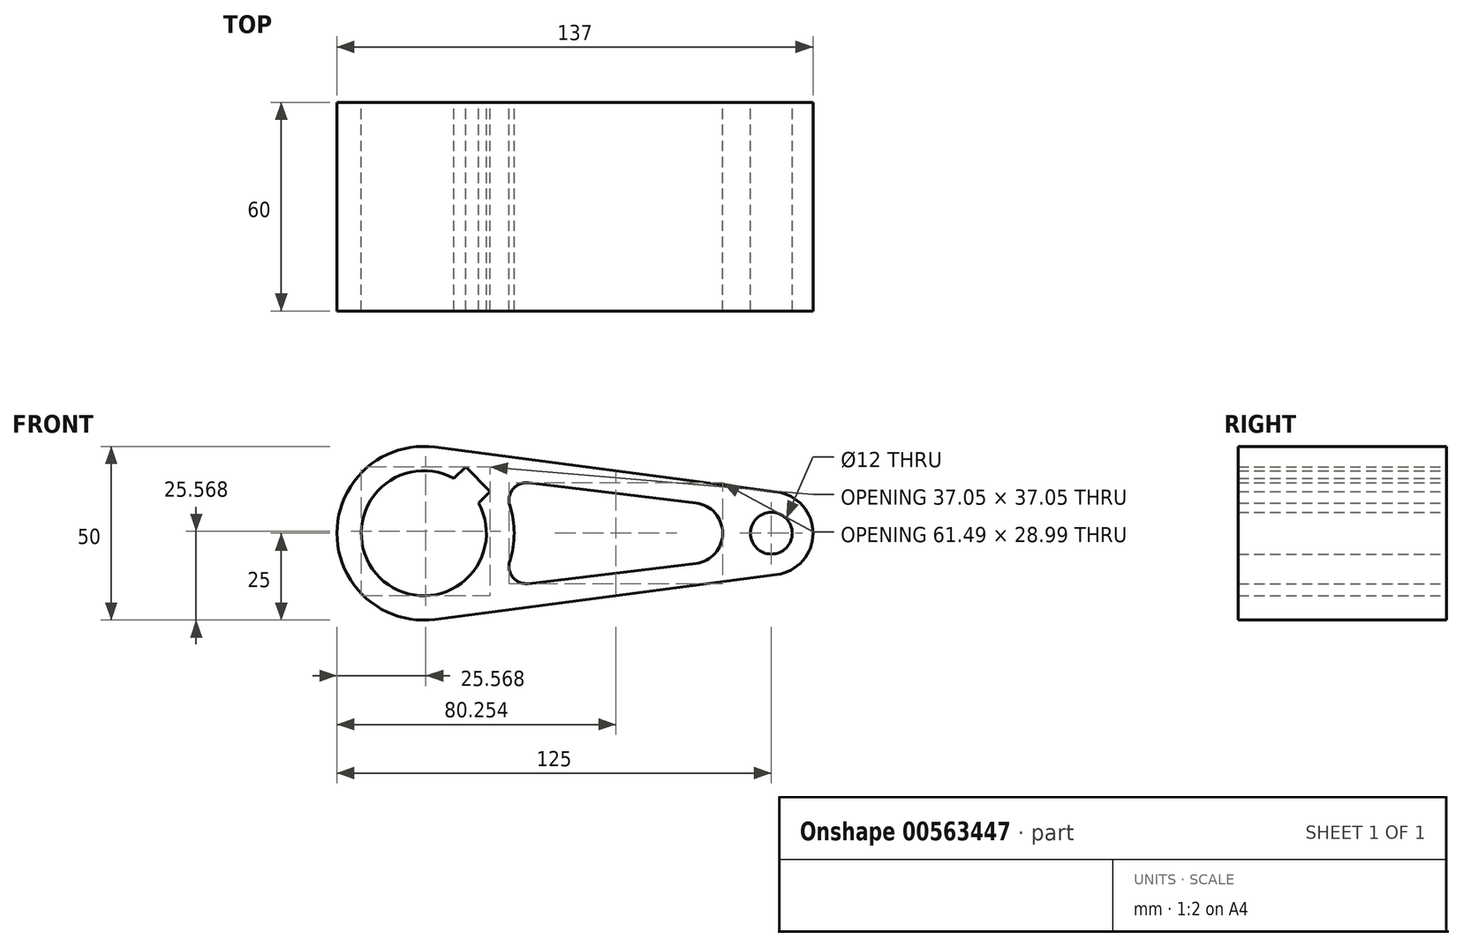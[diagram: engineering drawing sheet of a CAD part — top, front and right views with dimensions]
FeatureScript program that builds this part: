
annotation { "Feature Type Name" : "Feature", "Feature Type Description" : "" }
export const myFeature = defineFeature(function(context is Context, id is Id, definition is map)
    precondition{}
    {
        {
            var Q0;
            Q0=qCreatedBy(makeId("Front.planeOp"),FACE);
            var sketch = newSketch(context, id + "F0", { "sketchPlane" : qUnion([Q0])});
            skArc(sketch, "E0", {"start": v(3.25, 24.79) * mm, "mid": v(-25, 0) * mm, "end": v(3.25, -24.79) * mm});
            skArc(sketch, "E1", {"start": v(101.56, -11.9) * mm, "mid": v(112, 0) * mm, "end": v(101.56, 11.9) * mm});
            skLineSegment(sketch, "E2", {"start": v(3.25, 24.79) * mm, "end": v(101.56, 11.9) * mm});
            skLineSegment(sketch, "E3", {"start": v(3.25, -24.79) * mm, "end": v(101.56, -11.9) * mm});
            skLineSegment(sketch, "E4", {"start": v(0, 0) * mm, "end": v(15.56, 15.56) * mm, "construction": true});
            skLineSegment(sketch, "E5", {"start": v(15.56, 15.56) * mm, "end": v(19.1, 12.02) * mm});
            skLineSegment(sketch, "E6.MirrorCS", {"start": v(15.56, 15.56) * mm, "end": v(12.02, 19.1) * mm});
            skArc(sketch, "E7", {"start": v(8.7, 15.76) * mm, "mid": v(-12.73, -12.73) * mm, "end": v(15.76, 8.7) * mm});
            skLineSegment(sketch, "E8", {"start": v(12.02, 19.1) * mm, "end": v(8.7, 15.76) * mm});
            skLineSegment(sketch, "E9", {"start": v(19.1, 12.02) * mm, "end": v(15.76, 8.7) * mm});
            skCircle(sketch, "E10", {"center": v(100, 0) * mm, "radius": 6 * mm});
            skLineSegment(sketch, "E11", {"start": v(0, 0) * mm, "end": v(100, 0) * mm, "construction": true});
            skLineSegment(sketch, "E12", {"start": v(30.1, 14.5) * mm, "end": v(78.32, 8.66) * mm});
            skLineSegment(sketch, "E13", {"start": v(30.1, -14.5) * mm, "end": v(78.32, -8.66) * mm});
            skArc(sketch, "E14", {"start": v(78.32, -8.66) * mm, "mid": v(86, 0) * mm, "end": v(78.32, 8.66) * mm});
            skArc(sketch, "E15", {"start": v(30.1, 14.5) * mm, "mid": v(25.64, 12.7) * mm, "end": v(24.74, 8) * mm});
            skArc(sketch, "E16.MirrorC", {"start": v(30.1, -14.5) * mm, "mid": v(25.64, -12.7) * mm, "end": v(24.74, -8) * mm});
            skArc(sketch, "E17", {"start": v(24.74, -8) * mm, "mid": v(26, 0) * mm, "end": v(24.74, 8) * mm});
            skPoint(sketch, "E18.orphan", {"position": v(20.79, 15.62) * mm});
            skPoint(sketch, "E19.orphan", {"position": v(20.79, -15.62) * mm});
            skSolve(sketch);
        }
        {
            var Q0;
            Q0=makeQuery(id+"F0.imprint","IMPRINT",FACE,{"disambiguationData":[TD([[makeQuery(id+"F0.imprint","IMPRINT",EDGE,{"derivedFrom":sQuery(id+"F0.wireOp",EDGE,"E0")}),1.0]])]});
            extrude(context, id + "F1", {"entities" : qUnion([Q0]), "depth" : 60 * mm, "offsetDistance" : 25 * mm});
        }
    });
